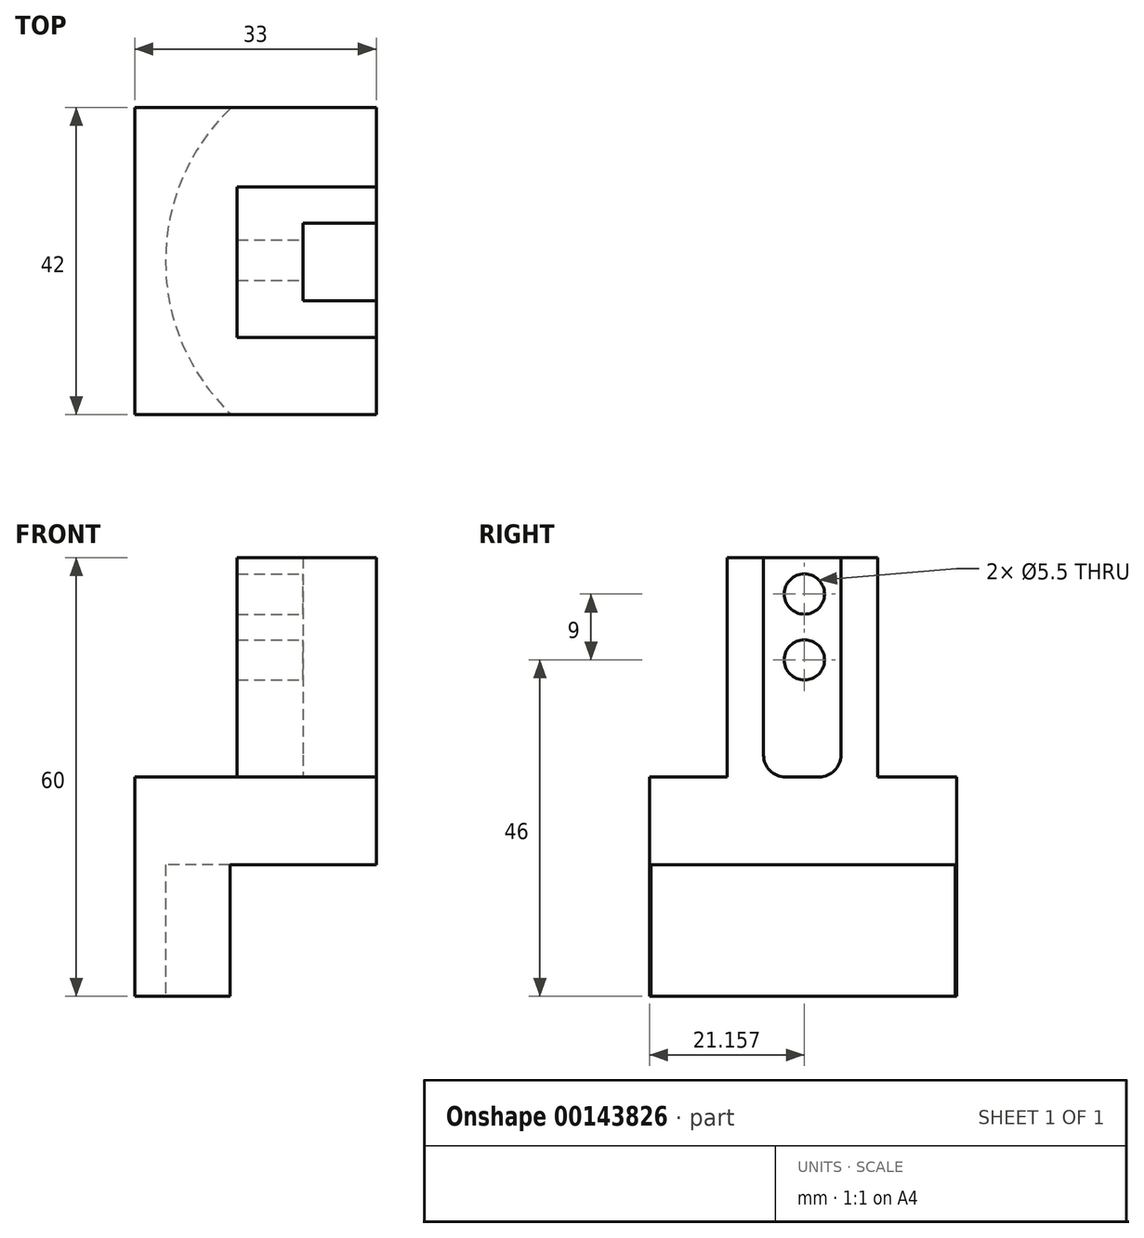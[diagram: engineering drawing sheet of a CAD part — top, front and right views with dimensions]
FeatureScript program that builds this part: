
annotation { "Feature Type Name" : "Feature", "Feature Type Description" : "" }
export const myFeature = defineFeature(function(context is Context, id is Id, definition is map)
    precondition{}
    {
        {
            var Q0;
            Q0=qCreatedBy(makeId("Front.planeOp"),FACE);
            var sketch = newSketch(context, id + "F0", { "sketchPlane" : qUnion([Q0])});
            skLineSegment(sketch, "E0.bottom", {"start": v(-3.5, -30) * mm, "end": v(-16.5, -30) * mm});
            skLineSegment(sketch, "E0.top", {"start": v(16.5, 30) * mm, "end": v(-2.5, 30) * mm});
            skLineSegment(sketch, "E0.left", {"start": v(16.5, -12) * mm, "end": v(16.5, 30) * mm});
            skLineSegment(sketch, "E0.right", {"start": v(-16.5, -30) * mm, "end": v(-16.5, 0) * mm});
            skPoint(sketch, "E0.middle", {"position": v(0, 0) * mm});
            skLineSegment(sketch, "E1", {"start": v(-16.5, 0) * mm, "end": v(0, 0) * mm});
            skLineSegment(sketch, "E2", {"start": v(16.5, -12) * mm, "end": v(-3.5, -12) * mm});
            skLineSegment(sketch, "E3", {"start": v(-3.5, -30) * mm, "end": v(-3.5, -12) * mm});
            skLineSegment(sketch, "E4", {"start": v(-2.5, 30) * mm, "end": v(-2.5, 0) * mm});
            skPoint(sketch, "E5.orphan", {"position": v(-16.5, 30) * mm});
            skPoint(sketch, "E6.orphan", {"position": v(16.5, -30) * mm});
            skPoint(sketch, "E7.orphan", {"position": v(-16.5, -12) * mm});
            skSolve(sketch);
        }
        {
            var Q0;
            Q0=makeQuery(id+"F0.imprint","IMPRINT",FACE,{"disambiguationData":[TD([[makeQuery(id+"F0.imprint","IMPRINT",EDGE,{"derivedFrom":sQuery(id+"F0.wireOp",EDGE,"E0.bottom")}),-1.0]])]});
            extrude(context, id + "F1", {"entities" : qUnion([Q0]), "depth" : 42 * mm});
        }
        {
            var Q0;
            Q0=makeQuery(id+"F1.opExtrude","SWEPT_FACE",FACE,{"disambiguationData":[OSD([sQuery(id+"F0.wireOp",EDGE,"E0.bottom")])]});
            var sketch = newSketch(context, id + "F2", { "sketchPlane" : qUnion([Q0])});
            skCircle(sketch, "E8", {"center": v(16.7, 21) * mm, "radius": 29 * mm});
            skSolve(sketch);
        }
        {
            var Q0;
            {var subQ0=sQuery(id+"F2.wireOp",EDGE,"E8");var subQ1=makeQuery(id+"F1.opExtrude","SWEPT_EDGE",EDGE,{"disambiguationData":[OSD([sQuery(id+"F0.wireOp",EDGE,"E0.bottom"),sQuery(id+"F0.wireOp",EDGE,"E3")])]});var subQ2=makeQuery(id+"F2.imprint","INTERSECT",VERTEX,{"disambiguationData":[OD(0.0)],"derivedFrom":[subQ1,subQ0]});Q0=makeQuery(id+"F2.imprint","IMPRINT",FACE,{"disambiguationData":[TD([[makeQuery(id+"F2.imprint","IMPRINT",EDGE,{"disambiguationData":[TD([[subQ2,1.0]])],"derivedFrom":subQ0}),1.0]])]});}
            extrude(context, id + "F3", {"entities" : qUnion([Q0]), "operationType" : NewBodyOperationType.REMOVE, "oppositeDirection" : true, "depth" : 18 * mm});
        }
        {
            var Q0;
            Q0=makeQuery(id+"F1.opExtrude","SWEPT_FACE",FACE,{"disambiguationData":[OSD([sQuery(id+"F0.wireOp",EDGE,"E0.left")])]});
            var sketch = newSketch(context, id + "F4", { "sketchPlane" : qUnion([Q0])});
            skLineSegment(sketch, "E9", {"start": v(-26, 30) * mm, "end": v(-26, 10.5) * mm});
            skLineSegment(sketch, "E10", {"start": v(-23, 7.5) * mm, "end": v(-19, 7.5) * mm});
            skLineSegment(sketch, "E11", {"start": v(-16, 10.5) * mm, "end": v(-16, 30) * mm});
            skLineSegment(sketch, "E12", {"start": v(-42, 0) * mm, "end": v(0, 0) * mm});
            skLineSegment(sketch, "E13", {"start": v(-31.43, 30) * mm, "end": v(-31.43, 0) * mm});
            skLineSegment(sketch, "E14", {"start": v(-10.84, 30) * mm, "end": v(-10.84, 0) * mm});
            skPoint(sketch, "E15.visualSharp", {"position": v(-26, 7.5) * mm});
            skArc(sketch, "E15.filletArc", {"start": v(-26, 10.5) * mm, "mid": v(-25.12, 8.38) * mm, "end": v(-23, 7.5) * mm});
            skPoint(sketch, "E16.visualSharp", {"position": v(-16, 7.5) * mm});
            skArc(sketch, "E16.filletArc", {"start": v(-19, 7.5) * mm, "mid": v(-16.88, 8.38) * mm, "end": v(-16, 10.5) * mm});
            skSolve(sketch);
        }
        {
            var Q0;
            {var subQ4=sQuery(id+"F4.wireOp",EDGE,"E13");Q0=makeQuery(id+"F4.imprint","IMPRINT",FACE,{"disambiguationData":[TD([[makeQuery(id+"F4.imprint","IMPRINT",EDGE,{"derivedFrom":subQ4}),-1.0]])]});}
            var Q1;
            {var subQ4=sQuery(id+"F4.wireOp",EDGE,"E14");Q1=makeQuery(id+"F4.imprint","IMPRINT",FACE,{"disambiguationData":[TD([[makeQuery(id+"F4.imprint","IMPRINT",EDGE,{"derivedFrom":subQ4}),1.0]])]});}
            extrude(context, id + "F5", {"entities" : qUnion([Q0, Q1]), "operationType" : NewBodyOperationType.REMOVE, "endBound" : BoundingType.UP_TO_NEXT, "oppositeDirection" : true, "depth" : 25 * mm});
        }
        {
            var Q0;
            Q0=makeQuery(id+"F1.opExtrude","SWEPT_FACE",FACE,{"disambiguationData":[OSD([sQuery(id+"F0.wireOp",EDGE,"E0.left")])]});
            var sketch = newSketch(context, id + "F6", { "sketchPlane" : qUnion([Q0])});
            skLineSegment(sketch, "E17", {"start": v(-26.43, 30) * mm, "end": v(-26.43, 3) * mm});
            skLineSegment(sketch, "E18", {"start": v(-15.84, 30) * mm, "end": v(-15.84, 3) * mm});
            skLineSegment(sketch, "E19", {"start": v(-18.84, 0) * mm, "end": v(-23.43, 0) * mm});
            skPoint(sketch, "E20.visualSharp", {"position": v(-26.43, 0) * mm});
            skArc(sketch, "E20.filletArc", {"start": v(-26.43, 3) * mm, "mid": v(-25.55, 0.88) * mm, "end": v(-23.43, 0) * mm});
            skPoint(sketch, "E21.visualSharp", {"position": v(-15.84, 0) * mm});
            skArc(sketch, "E21.filletArc", {"start": v(-18.84, 0) * mm, "mid": v(-16.72, 0.88) * mm, "end": v(-15.84, 3) * mm});
            skSolve(sketch);
        }
        {
            var Q0;
            {var subQ1=sQuery(id+"F6.wireOp",EDGE,"E17");Q0=makeQuery(id+"F6.imprint","IMPRINT",FACE,{"disambiguationData":[TD([[makeQuery(id+"F6.imprint","IMPRINT",EDGE,{"derivedFrom":subQ1}),1.0]])]});}
            extrude(context, id + "F7", {"entities" : qUnion([Q0]), "operationType" : NewBodyOperationType.REMOVE, "oppositeDirection" : true, "depth" : 10 * mm});
        }
        {
            var Q0;
            Q0=makeQuery(id+"F7.boolean.opBoolean","COPY",FACE,{"derivedFrom":makeQuery(id+"F7.opExtrude","CAP_FACE",FACE,{"disambiguationData":[OSD([sQuery(id+"F0.wireOp",EDGE,"E0.top"),sQuery(id+"F0.wireOp",EDGE,"E0.left"),sQuery(id+"F6.wireOp",EDGE,"E17"),sQuery(id+"F6.wireOp",EDGE,"E18"),sQuery(id+"F6.wireOp",EDGE,"E19"),sQuery(id+"F6.wireOp",EDGE,"E20.filletArc"),sQuery(id+"F6.wireOp",EDGE,"E21.filletArc")])],"isStart":false})});
            var sketch = newSketch(context, id + "F8", { "sketchPlane" : qUnion([Q0])});
            skCircle(sketch, "E22", {"center": v(-20.84, 25) * mm, "radius": 2.25 * mm});
            skCircle(sketch, "E23", {"center": v(-20.84, 16) * mm, "radius": 2.25 * mm});
            skSolve(sketch);
        }
        {
            var Q0;
            Q0=sQuery(id+"F8.wireOp",VERTEX,"E22.center");
            var Q1;
            Q1=sQuery(id+"F8.wireOp",VERTEX,"E23.center");
            var Q2;
            Q2=makeQuery(id+"F1.opExtrude","SWEPT_BODY",BODY,{"disambiguationData":[OSD([sQuery(id+"F0.wireOp",EDGE,"E0.bottom"),sQuery(id+"F0.wireOp",EDGE,"E0.top"),sQuery(id+"F0.wireOp",EDGE,"E0.left"),sQuery(id+"F0.wireOp",EDGE,"E0.right"),sQuery(id+"F0.wireOp",EDGE,"E1"),sQuery(id+"F0.wireOp",EDGE,"E2"),sQuery(id+"F0.wireOp",EDGE,"E3"),sQuery(id+"F0.wireOp",EDGE,"E4")])]});
            hole(context, id + "F9", {"style" : HoleStyle.SIMPLE, "endStyle" : HoleEndStyle.THROUGH, "holeDiameter" : 5.5 * mm, "startFromSketch" : true, "locations" : qUnion([Q0, Q1]), "scope" : qUnion([Q2]), "isTappedThrough" : true});
        }
    });
